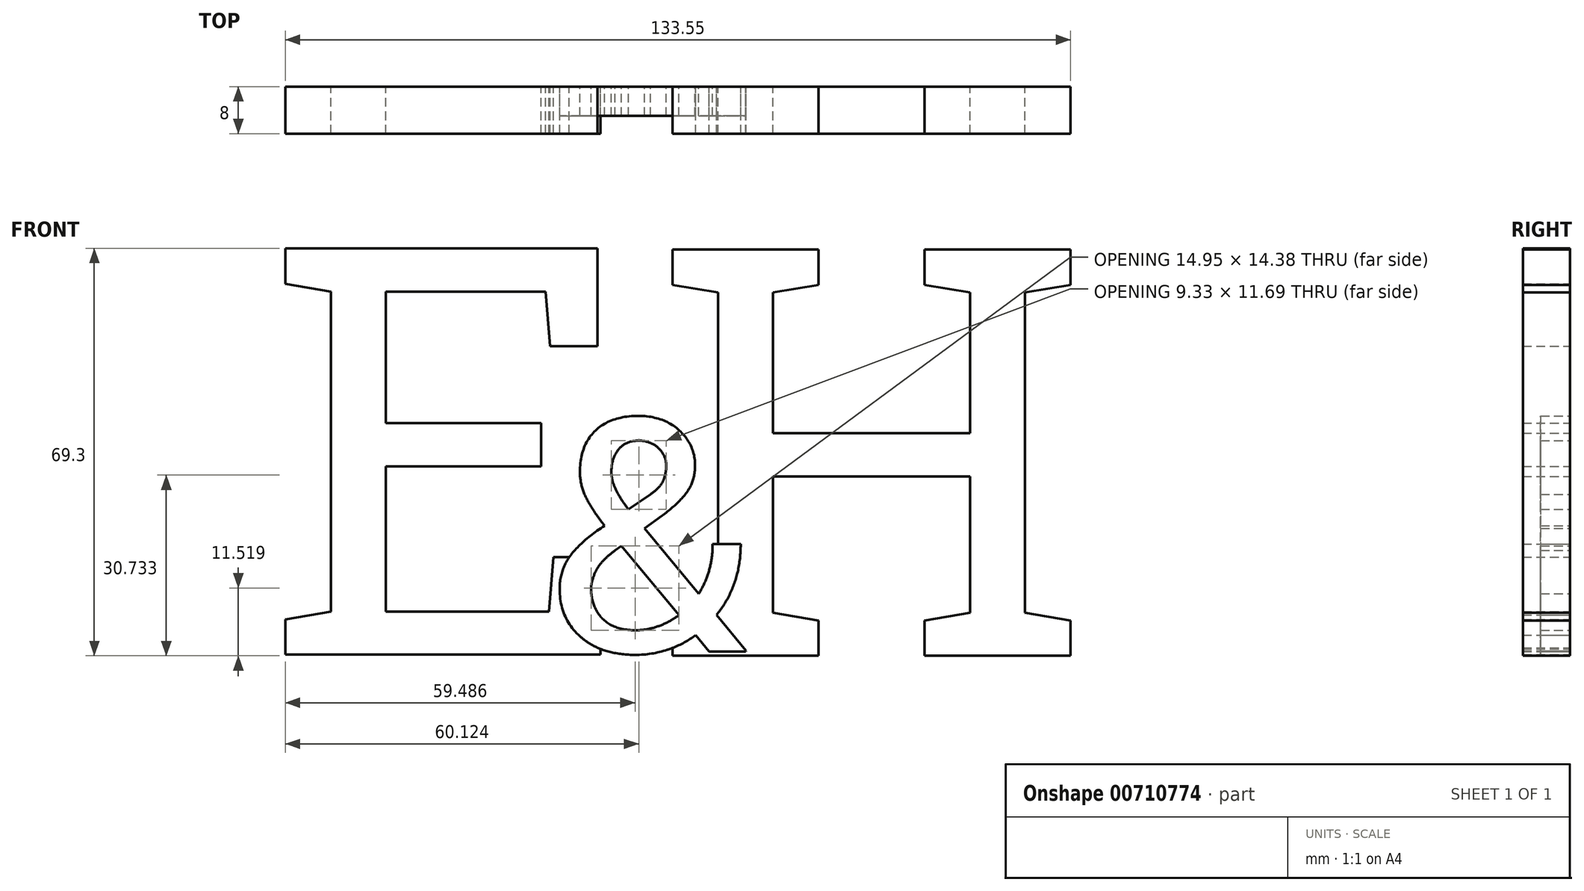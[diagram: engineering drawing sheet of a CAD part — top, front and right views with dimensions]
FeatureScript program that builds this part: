
annotation { "Feature Type Name" : "Feature", "Feature Type Description" : "" }
export const myFeature = defineFeature(function(context is Context, id is Id, definition is map)
    precondition{}
    {
        {
            var Q0;
            Q0=qCreatedBy(makeId("Front.planeOp"),FACE);
            var sketch = newSketch(context, id + "F0", { "sketchPlane" : qUnion([Q0])});
            skText(sketch, "E0", { "text": "E", "fontName": "RobotoSlab-Regular.ttf"});
            skText(sketch, "E1", { "text": "&", "fontName": "RobotoSlab-Regular.ttf"});
            skText(sketch, "E2", { "text": "H", "fontName": "RobotoSlab-Regular.ttf"});
            const initialGuessF0  = {"E0": [-0.20492, 0.04894, 1, 0, 0.07], "E1": [-0.15689, 0.04948, 1, 0, 0.04], "E2": [-0.13906, 0.04876, 1, 0, 0.07]};
            skSetInitialGuess(sketch, initialGuessF0);
            skSolve(sketch);
        }
        {
            var Q0;
            Q0=makeQuery(id+"F0.imprint","IMPRINT",FACE,{"disambiguationData":[TD([[makeQuery(id+"F0.imprint","IMPRINT",EDGE,{"derivedFrom":sQuery(id+"F0.wireOp",EDGE,"E0.sketch_text.stroke-0")}),-1.0]])]});
            var Q1;
            {var subQ0=sQuery(id+"F0.wireOp",EDGE,"E1.sketch_text.stroke-15");Q1=makeQuery(id+"F0.imprint","IMPRINT",FACE,{"disambiguationData":[TD([[makeQuery(id+"F0.imprint","IMPRINT",EDGE,{"derivedFrom":subQ0}),1.0]])]});}
            extrude(context, id + "F1", {"entities" : qUnion([Q0, Q1]), "depth" : 8 * mm, "offsetDistance" : 25 * mm});
        }
        {
            var Q0;
            {var subQ8=sQuery(id+"F0.wireOp",EDGE,"E1.sketch_text.stroke-1");Q0=makeQuery(id+"F0.imprint","IMPRINT",FACE,{"disambiguationData":[TD([[makeQuery(id+"F0.imprint","IMPRINT",EDGE,{"derivedFrom":subQ8}),-1.0]])]});}
            var Q1;
            {var subQ5=sQuery(id+"F0.wireOp",EDGE,"E1.sketch_text.stroke-15");Q1=makeQuery(id+"F0.imprint","IMPRINT",FACE,{"disambiguationData":[TD([[makeQuery(id+"F0.imprint","IMPRINT",EDGE,{"derivedFrom":subQ5}),-1.0]])]});}
            var Q2;
            {var subQ5=sQuery(id+"F0.wireOp",EDGE,"E1.sketch_text.stroke-24");Q2=makeQuery(id+"F0.imprint","IMPRINT",FACE,{"disambiguationData":[TD([[makeQuery(id+"F0.imprint","IMPRINT",EDGE,{"derivedFrom":subQ5}),-1.0]])]});}
            extrude(context, id + "F2", {"entities" : qUnion([Q0, Q1, Q2]), "depth" : 5 * mm, "offsetDistance" : 25 * mm});
        }
    });
